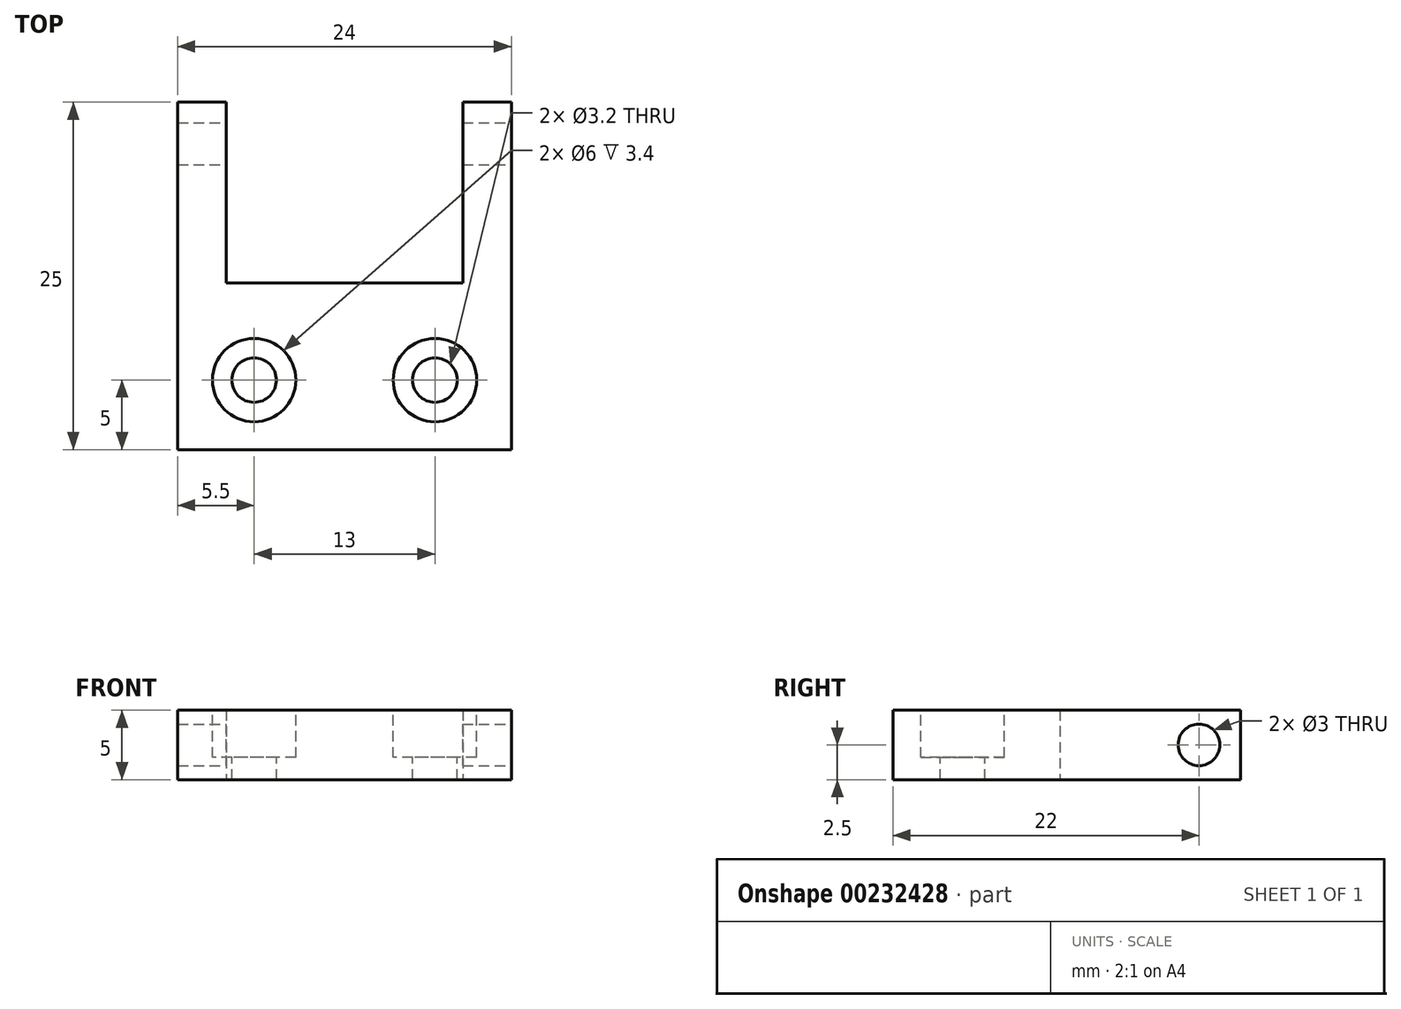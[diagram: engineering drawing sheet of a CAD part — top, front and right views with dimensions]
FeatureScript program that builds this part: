
annotation { "Feature Type Name" : "Feature", "Feature Type Description" : "" }
export const myFeature = defineFeature(function(context is Context, id is Id, definition is map)
    precondition{}
    {
        {
            var Q0;
            Q0=qCreatedBy(makeId("Top.planeOp"),FACE);
            var sketch = newSketch(context, id + "F0", { "sketchPlane" : qUnion([Q0])});
            skLineSegment(sketch, "E0.bottom", {"start": v(12, 12.5) * mm, "end": v(8.5, 12.5) * mm});
            skLineSegment(sketch, "E0.top", {"start": v(12, -12.5) * mm, "end": v(-12, -12.5) * mm});
            skLineSegment(sketch, "E0.left", {"start": v(12, 12.5) * mm, "end": v(12, -12.5) * mm});
            skLineSegment(sketch, "E0.right", {"start": v(-12, 12.5) * mm, "end": v(-12, -12.5) * mm});
            skPoint(sketch, "E0.middle", {"position": v(0, 0) * mm});
            skLineSegment(sketch, "E1.top", {"start": v(-8.5, -0.5) * mm, "end": v(8.5, -0.5) * mm});
            skLineSegment(sketch, "E1.left", {"start": v(-8.5, 12.5) * mm, "end": v(-8.5, -0.5) * mm});
            skLineSegment(sketch, "E1.right", {"start": v(8.5, 12.5) * mm, "end": v(8.5, -0.5) * mm});
            skPoint(sketch, "E2", {"position": v(-6.5, -7.5) * mm});
            skPoint(sketch, "E3", {"position": v(6.5, -7.5) * mm});
            skLineSegment(sketch, "E4.trimOffspring", {"start": v(-8.5, 12.5) * mm, "end": v(-12, 12.5) * mm});
            skSolve(sketch);
        }
        {
            var Q0;
            Q0=makeQuery(id+"F0.imprint","IMPRINT",FACE,{"disambiguationData":[TD([[makeQuery(id+"F0.imprint","IMPRINT",EDGE,{"derivedFrom":sQuery(id+"F0.wireOp",EDGE,"E0.bottom")}),1.0]])]});
            extrude(context, id + "F1", {"entities" : qUnion([Q0]), "endBound" : BoundingType.SYMMETRIC, "depth" : 5 * mm});
        }
        {
            var Q0;
            Q0=makeQuery(id+"F1.opExtrude","CAP_FACE",FACE,{"disambiguationData":[OSD([sQuery(id+"F0.wireOp",EDGE,"E0.bottom"),sQuery(id+"F0.wireOp",EDGE,"E0.top"),sQuery(id+"F0.wireOp",EDGE,"E0.left"),sQuery(id+"F0.wireOp",EDGE,"E0.right"),sQuery(id+"F0.wireOp",EDGE,"E1.top"),sQuery(id+"F0.wireOp",EDGE,"E1.left"),sQuery(id+"F0.wireOp",EDGE,"E1.right"),sQuery(id+"F0.wireOp",EDGE,"E4.trimOffspring")])],"isStart":false});
            var sketch = newSketch(context, id + "F2", { "sketchPlane" : qUnion([Q0])});
            skPoint(sketch, "E5", {"position": v(-6.5, -7.5) * mm});
            skPoint(sketch, "E6", {"position": v(6.5, -7.5) * mm});
            skSolve(sketch);
        }
        {
            var Q0;
            Q0=sQuery(id+"F2.wireOp",VERTEX,"E5");
            var Q1;
            Q1=sQuery(id+"F2.wireOp",VERTEX,"E6");
            var Q2;
            Q2=makeQuery(id+"F1.opExtrude","SWEPT_BODY",BODY,{"disambiguationData":[OSD([sQuery(id+"F0.wireOp",EDGE,"E0.bottom"),sQuery(id+"F0.wireOp",EDGE,"E0.top"),sQuery(id+"F0.wireOp",EDGE,"E0.left"),sQuery(id+"F0.wireOp",EDGE,"E0.right"),sQuery(id+"F0.wireOp",EDGE,"E1.top"),sQuery(id+"F0.wireOp",EDGE,"E1.left"),sQuery(id+"F0.wireOp",EDGE,"E1.right"),sQuery(id+"F0.wireOp",EDGE,"E4.trimOffspring")])]});
            hole(context, id + "F3", {"style" : HoleStyle.C_BORE, "endStyle" : HoleEndStyle.THROUGH, "holeDiameter" : 3.2 * mm, "cBoreDiameter" : 6 * mm, "cBoreDepth" : 3.4 * mm, "startFromSketch" : true, "locations" : qUnion([Q0, Q1]), "scope" : qUnion([Q2]), "isTappedThrough" : true});
        }
        {
            var Q0;
            Q0=makeQuery(id+"F1.opExtrude","SWEPT_FACE",FACE,{"disambiguationData":[OSD([sQuery(id+"F0.wireOp",EDGE,"E0.left")])]});
            var sketch = newSketch(context, id + "F4", { "sketchPlane" : qUnion([Q0])});
            skPoint(sketch, "E7", {"position": v(9.5, 0) * mm});
            skSolve(sketch);
        }
        {
            var Q0;
            Q0=sQuery(id+"F4.wireOp",VERTEX,"E7");
            var Q1;
            Q1=makeQuery(id+"F1.opExtrude","SWEPT_BODY",BODY,{"disambiguationData":[OSD([sQuery(id+"F0.wireOp",EDGE,"E0.bottom"),sQuery(id+"F0.wireOp",EDGE,"E0.top"),sQuery(id+"F0.wireOp",EDGE,"E0.left"),sQuery(id+"F0.wireOp",EDGE,"E0.right"),sQuery(id+"F0.wireOp",EDGE,"E1.top"),sQuery(id+"F0.wireOp",EDGE,"E1.left"),sQuery(id+"F0.wireOp",EDGE,"E1.right"),sQuery(id+"F0.wireOp",EDGE,"E4.trimOffspring")])]});
            hole(context, id + "F5", {"style" : HoleStyle.SIMPLE, "endStyle" : HoleEndStyle.THROUGH, "holeDiameter" : 3 * mm, "startFromSketch" : true, "locations" : qUnion([Q0]), "scope" : qUnion([Q1]), "isTappedThrough" : true});
        }
    });
